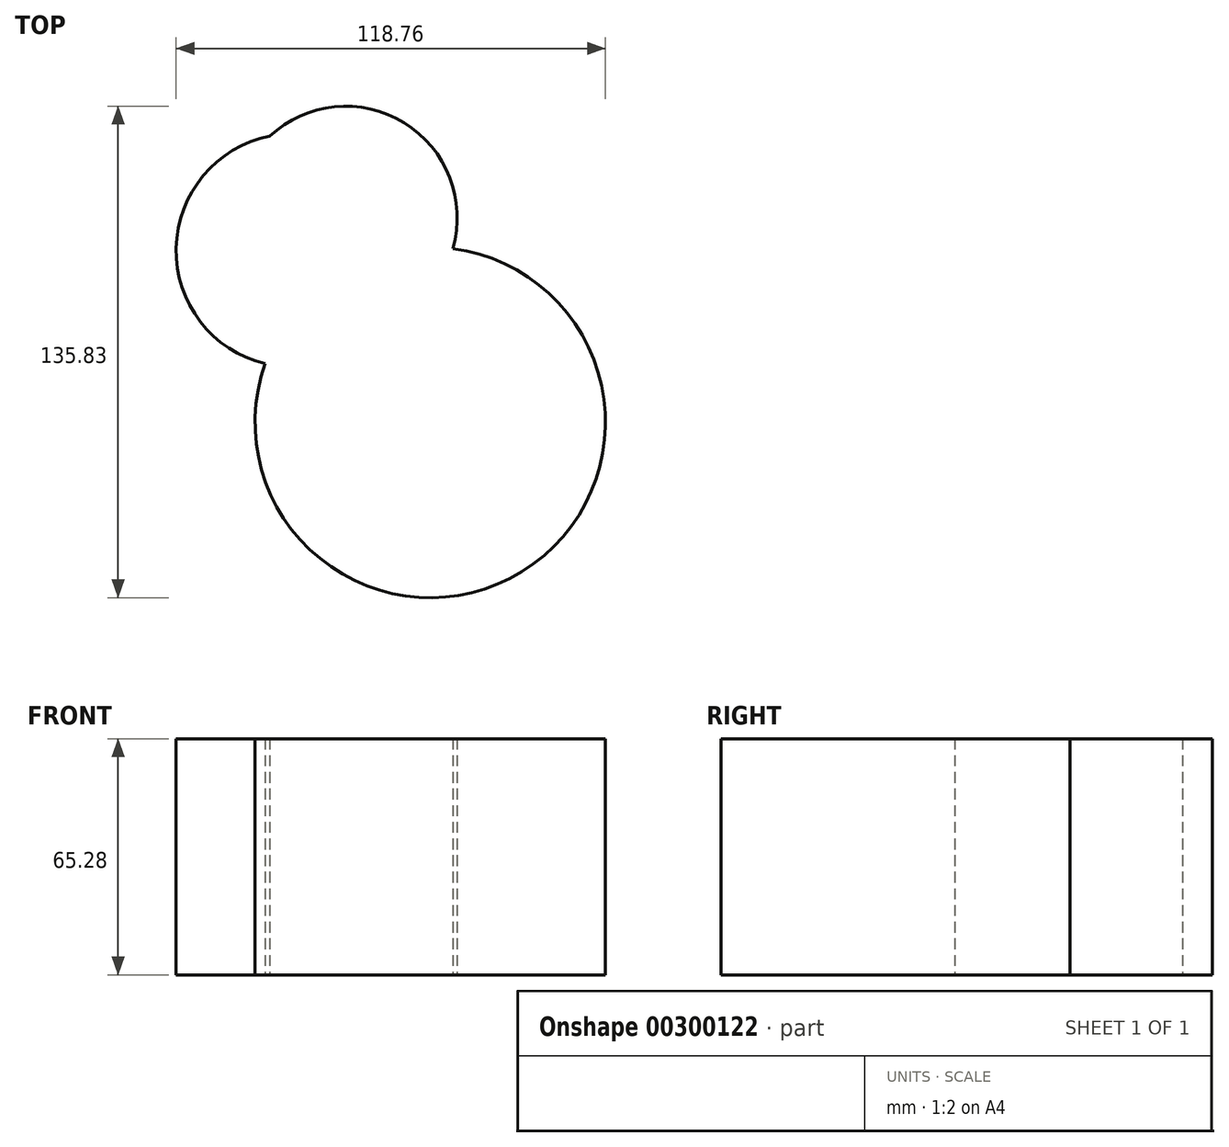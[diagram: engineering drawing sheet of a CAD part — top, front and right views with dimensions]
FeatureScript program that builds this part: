
annotation { "Feature Type Name" : "Feature", "Feature Type Description" : "" }
export const myFeature = defineFeature(function(context is Context, id is Id, definition is map)
    precondition{}
    {
        {
            var Q0;
            Q0=qCreatedBy(makeId("Top.planeOp"),FACE);
            var sketch = newSketch(context, id + "F0", { "sketchPlane" : qUnion([Q0])});
            skArc(sketch, "E0", {"start": v(-6.28, 31.58) * mm, "mid": v(-32.2, 0.66) * mm, "end": v(-7.57, -31.3) * mm});
            skArc(sketch, "E1", {"start": v(44.35, 0.55) * mm, "mid": v(30.85, 35.32) * mm, "end": v(-6.28, 31.58) * mm});
            skArc(sketch, "E2", {"start": v(-7.57, -31.3) * mm, "mid": v(63.43, -88.81) * mm, "end": v(44.35, 0.55) * mm});
            skSolve(sketch);
        }
        {
            var Q0;
            Q0=makeQuery(id+"F0.imprint","IMPRINT",FACE,{"disambiguationData":[TD([[makeQuery(id+"F0.imprint","IMPRINT",EDGE,{"derivedFrom":sQuery(id+"F0.wireOp",EDGE,"E0")}),1.0]])]});
            extrude(context, id + "F1", {"entities" : qUnion([Q0]), "depth" : 65.28 * mm});
        }
    });
